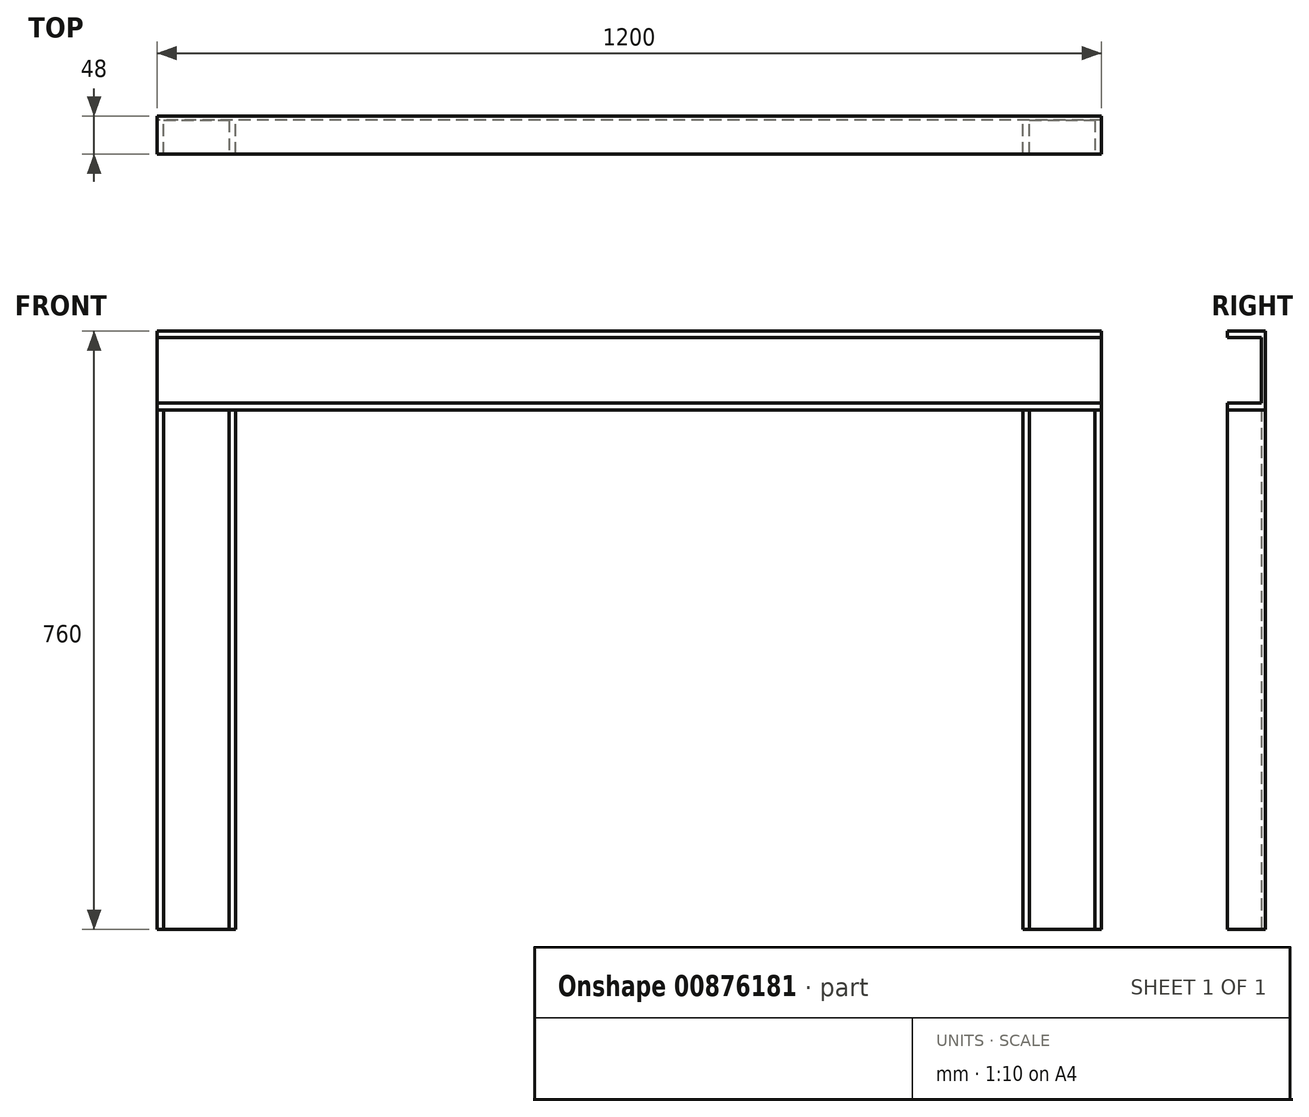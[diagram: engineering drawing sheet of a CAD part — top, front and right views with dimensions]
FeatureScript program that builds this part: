
annotation { "Feature Type Name" : "Feature", "Feature Type Description" : "" }
export const myFeature = defineFeature(function(context is Context, id is Id, definition is map)
    precondition{}
    {
        {
            var Q0;
            Q0=qCreatedBy(makeId("Top.planeOp"),FACE);
            var sketch = newSketch(context, id + "F0", { "sketchPlane" : qUnion([Q0])});
            skLineSegment(sketch, "E0.bottom", {"start": v(50, -24) * mm, "end": v(-50, -24) * mm});
            skLineSegment(sketch, "E0.top", {"start": v(50, 24) * mm, "end": v(-50, 24) * mm});
            skLineSegment(sketch, "E0.left", {"start": v(50, -24) * mm, "end": v(50, 24) * mm});
            skLineSegment(sketch, "E0.right", {"start": v(-50, -24) * mm, "end": v(-50, 24) * mm});
            skPoint(sketch, "E0.middle", {"position": v(0, 0) * mm});
            skLineSegment(sketch, "E1", {"start": v(-41.5, -24) * mm, "end": v(-41.5, 18.7) * mm});
            skLineSegment(sketch, "E2", {"start": v(-41.5, 18.7) * mm, "end": v(41.5, 18.7) * mm});
            skLineSegment(sketch, "E3", {"start": v(41.5, 18.7) * mm, "end": v(41.5, -24) * mm});
            skSolve(sketch);
        }
        {
            var Q0;
            Q0=qCreatedBy(makeId("Top.planeOp"),FACE);
            var sketch = newSketch(context, id + "F1", { "sketchPlane" : qUnion([Q0])});
            skLineSegment(sketch, "E4.bottom", {"start": v(-1050, -24) * mm, "end": v(-1150, -24) * mm});
            skLineSegment(sketch, "E4.top", {"start": v(-1050, 24) * mm, "end": v(-1150, 24) * mm});
            skLineSegment(sketch, "E4.left", {"start": v(-1050, -24) * mm, "end": v(-1050, 24) * mm});
            skLineSegment(sketch, "E4.right", {"start": v(-1150, -24) * mm, "end": v(-1150, 24) * mm});
            skPoint(sketch, "E4.middle", {"position": v(-1100, 0) * mm});
            skLineSegment(sketch, "E5", {"start": v(-1141.5, -24) * mm, "end": v(-1141.5, 18.7) * mm});
            skLineSegment(sketch, "E6", {"start": v(-1141.5, 18.7) * mm, "end": v(-1058.5, 18.7) * mm});
            skLineSegment(sketch, "E7", {"start": v(-1058.5, 18.7) * mm, "end": v(-1058.5, -24) * mm});
            skSolve(sketch);
        }
        {
            var Q0;
            Q0=makeQuery(id+"F1.imprint","IMPRINT",FACE,{"disambiguationData":[TD([[makeQuery(id+"F1.imprint","IMPRINT",EDGE,{"derivedFrom":sQuery(id+"F1.wireOp",EDGE,"E4.top")}),1.0]])]});
            var Q1;
            Q1=makeQuery(id+"F0.imprint","IMPRINT",FACE,{"disambiguationData":[TD([[makeQuery(id+"F0.imprint","IMPRINT",EDGE,{"derivedFrom":sQuery(id+"F0.wireOp",EDGE,"E0.top")}),1.0]])]});
            extrude(context, id + "F2", {"entities" : qUnion([Q0, Q1]), "depth" : 660 * mm, "offsetDistance" : 25 * mm});
        }
        {
            var Q0;
            Q0=makeQuery(id+"F2.opExtrude","SWEPT_FACE",FACE,{"disambiguationData":[OSD([sQuery(id+"F1.wireOp",EDGE,"E4.right")])]});
            cPlane(context, id + "F3", {"entities" : qUnion([Q0]), "cplaneType" : CPlaneType.OFFSET, "offset" : 0 * mm, "width" : 150 * mm, "height" : 150 * mm});
        }
        {
            var Q0;
            Q0=qCreatedBy(id+"F3.planeOp",FACE);
            var sketch = newSketch(context, id + "F4", { "sketchPlane" : qUnion([Q0])});
            skLineSegment(sketch, "E8.bottom", {"start": v(-24, 660) * mm, "end": v(24, 660) * mm});
            skLineSegment(sketch, "E8.top", {"start": v(-24, 760) * mm, "end": v(24, 760) * mm});
            skLineSegment(sketch, "E8.left", {"start": v(-24, 660) * mm, "end": v(-24, 760) * mm});
            skLineSegment(sketch, "E8.right", {"start": v(24, 660) * mm, "end": v(24, 760) * mm});
            skLineSegment(sketch, "E9", {"start": v(24, 668.5) * mm, "end": v(-18.7, 668.5) * mm});
            skLineSegment(sketch, "E10", {"start": v(-18.7, 668.5) * mm, "end": v(-18.7, 751.5) * mm});
            skLineSegment(sketch, "E11", {"start": v(-18.7, 751.5) * mm, "end": v(24, 751.5) * mm});
            skSolve(sketch);
        }
        {
            var Q0;
            {var subQ1=sQuery(id+"F4.wireOp",EDGE,"E8.bottom");Q0=makeQuery(id+"F4.imprint","IMPRINT",FACE,{"disambiguationData":[TD([[makeQuery(id+"F4.imprint","IMPRINT",EDGE,{"derivedFrom":subQ1}),1.0]])]});}
            var Q1;
            Q1=makeQuery(id+"F2.opExtrude","SWEPT_FACE",FACE,{"disambiguationData":[OSD([sQuery(id+"F0.wireOp",EDGE,"E0.left")])]});
            extrude(context, id + "F5", {"entities" : qUnion([Q0]), "endBound" : BoundingType.UP_TO_SURFACE, "oppositeDirection" : true, "depth" : 25 * mm, "endBoundEntityFace" : qUnion([Q1]), "offsetDistance" : 25 * mm});
        }
    });
